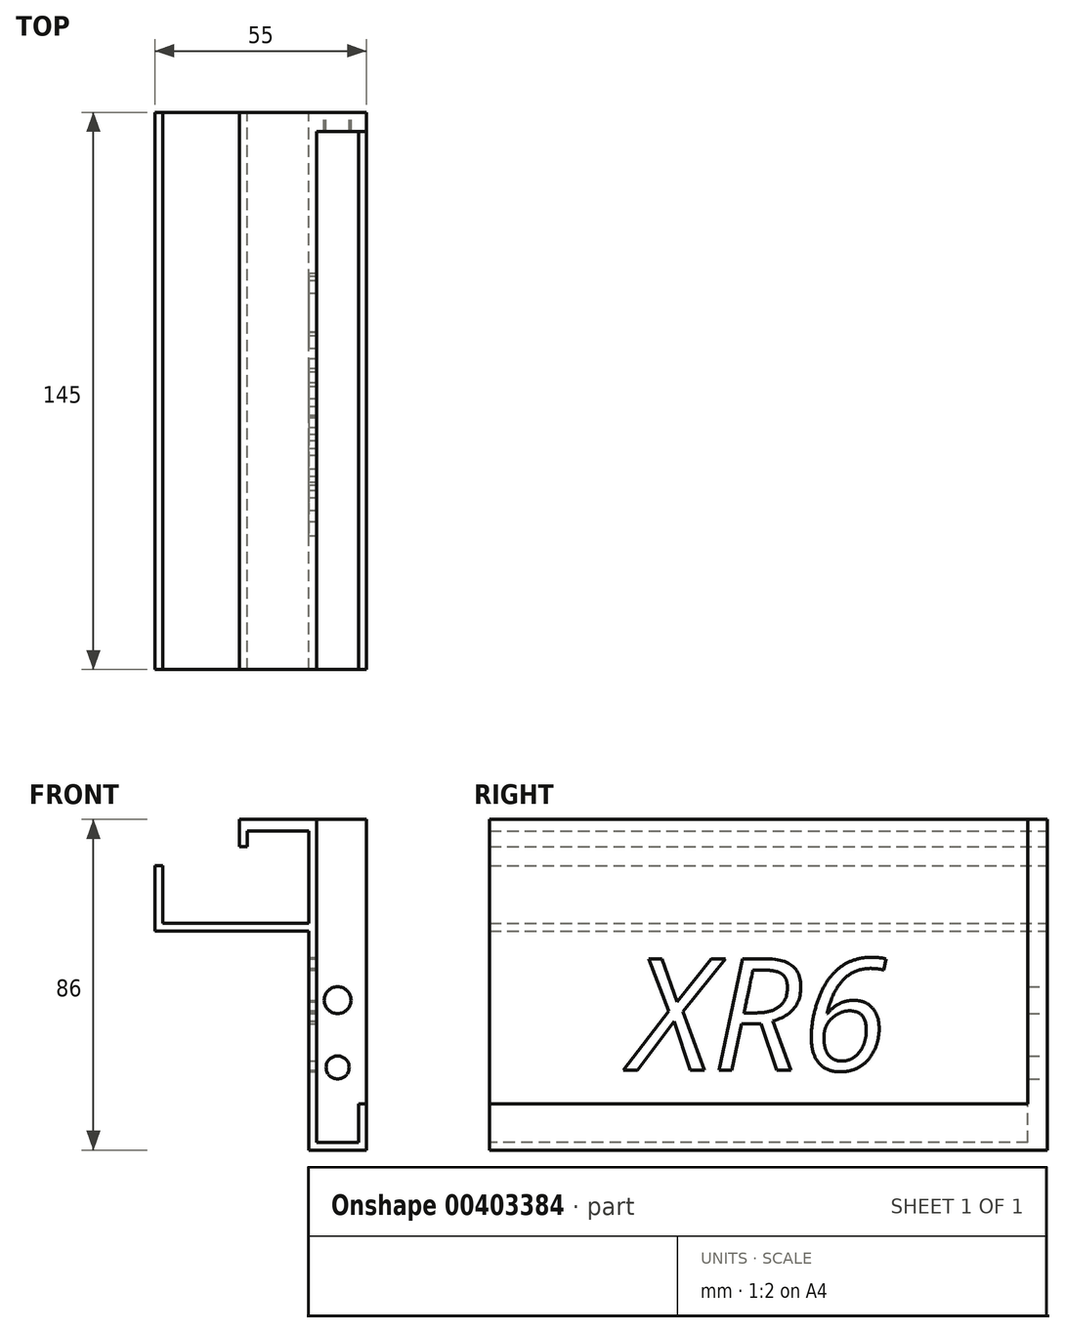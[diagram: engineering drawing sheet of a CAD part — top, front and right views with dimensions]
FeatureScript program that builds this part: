
annotation { "Feature Type Name" : "Feature", "Feature Type Description" : "" }
export const myFeature = defineFeature(function(context is Context, id is Id, definition is map)
    precondition{}
    {
        {
            var Q0;
            Q0=qCreatedBy(makeId("Front.planeOp"),FACE);
            var sketch = newSketch(context, id + "F0", { "sketchPlane" : qUnion([Q0])});
            skLineSegment(sketch, "E0", {"start": v(0, -43) * mm, "end": v(15, -43) * mm});
            skLineSegment(sketch, "E1", {"start": v(15, -43) * mm, "end": v(15, -31) * mm});
            skLineSegment(sketch, "E2", {"start": v(2, 43) * mm, "end": v(-18, 43) * mm});
            skLineSegment(sketch, "E3", {"start": v(-18, 43) * mm, "end": v(-18, 36) * mm});
            skLineSegment(sketch, "E4", {"start": v(-18, 36) * mm, "end": v(-16, 36) * mm});
            skLineSegment(sketch, "E5", {"start": v(-16, 36) * mm, "end": v(-16, 40) * mm});
            skLineSegment(sketch, "E6", {"start": v(-16, 40) * mm, "end": v(0, 40) * mm});
            skLineSegment(sketch, "E7", {"start": v(0, 40) * mm, "end": v(0, 16) * mm});
            skLineSegment(sketch, "E8", {"start": v(0, 16) * mm, "end": v(-38, 16) * mm});
            skLineSegment(sketch, "E9", {"start": v(-38, 16) * mm, "end": v(-38, 31) * mm});
            skLineSegment(sketch, "E10", {"start": v(-38, 31) * mm, "end": v(-40, 31) * mm});
            skLineSegment(sketch, "E11", {"start": v(-40, 31) * mm, "end": v(-40, 14) * mm});
            skLineSegment(sketch, "E12", {"start": v(-40, 14) * mm, "end": v(0, 14) * mm});
            skLineSegment(sketch, "E13", {"start": v(0, 14) * mm, "end": v(0, -43) * mm});
            skLineSegment(sketch, "E14", {"start": v(15, -31) * mm, "end": v(2, -31) * mm});
            skLineSegment(sketch, "E15", {"start": v(2, -31) * mm, "end": v(2, 43) * mm});
            skSolve(sketch);
        }
        {
            var Q0;
            Q0=makeQuery(id+"F0.imprint","IMPRINT",FACE,{"disambiguationData":[TD([[makeQuery(id+"F0.imprint","IMPRINT",EDGE,{"derivedFrom":sQuery(id+"F0.wireOp",EDGE,"E0")}),1.0]])]});
            extrude(context, id + "F1", {"entities" : qUnion([Q0]), "depth" : 145 * mm});
        }
        {
            var Q0;
            Q0=makeQuery(id+"F1.opExtrude","CAP_FACE",FACE,{"disambiguationData":[OSD([sQuery(id+"F0.wireOp",EDGE,"E0"),sQuery(id+"F0.wireOp",EDGE,"E1"),sQuery(id+"F0.wireOp",EDGE,"E2"),sQuery(id+"F0.wireOp",EDGE,"E3"),sQuery(id+"F0.wireOp",EDGE,"E4"),sQuery(id+"F0.wireOp",EDGE,"E5"),sQuery(id+"F0.wireOp",EDGE,"E6"),sQuery(id+"F0.wireOp",EDGE,"E7"),sQuery(id+"F0.wireOp",EDGE,"E8"),sQuery(id+"F0.wireOp",EDGE,"E9"),sQuery(id+"F0.wireOp",EDGE,"E10"),sQuery(id+"F0.wireOp",EDGE,"E11"),sQuery(id+"F0.wireOp",EDGE,"E12"),sQuery(id+"F0.wireOp",EDGE,"E13"),sQuery(id+"F0.wireOp",EDGE,"E14"),sQuery(id+"F0.wireOp",EDGE,"E15")])],"isStart":false});
            var sketch = newSketch(context, id + "F2", { "sketchPlane" : qUnion([Q0])});
            skLineSegment(sketch, "E16", {"start": v(13, -31) * mm, "end": v(13, -41) * mm});
            skLineSegment(sketch, "E17", {"start": v(13, -41) * mm, "end": v(2, -41) * mm});
            skLineSegment(sketch, "E18", {"start": v(2, -41) * mm, "end": v(2, -31) * mm});
            skLineSegment(sketch, "E19", {"start": v(2, -31) * mm, "end": v(13, -31) * mm});
            skSolve(sketch);
        }
        {
            var Q0;
            Q0=makeQuery(id+"F2.imprint","IMPRINT",FACE,{"disambiguationData":[TD([[makeQuery(id+"F2.imprint","IMPRINT",EDGE,{"derivedFrom":sQuery(id+"F2.wireOp",EDGE,"E16")}),-1.0]])]});
            extrude(context, id + "F3", {"entities" : qUnion([Q0]), "operationType" : NewBodyOperationType.REMOVE, "oppositeDirection" : true, "depth" : 140 * mm});
        }
        {
            var Q0;
            Q0=makeQuery(id+"F3.boolean.opBoolean","MERGE",FACE,{"derivedFrom":[makeQuery(id+"F1.opExtrude","SWEPT_FACE",FACE,{"disambiguationData":[OSD([sQuery(id+"F0.wireOp",EDGE,"E15")])]}),makeQuery(id+"F3.opExtrude","SWEPT_FACE",FACE,{"disambiguationData":[OSD([sQuery(id+"F2.wireOp",EDGE,"E18")])]})]});
            var sketch = newSketch(context, id + "F4", { "sketchPlane" : qUnion([Q0])});
            skLineSegment(sketch, "E20", {"start": v(0, 43) * mm, "end": v(-5, 43) * mm});
            skSolve(sketch);
        }
        {
            var Q0;
            {var subQ4=sQuery(id+"F4.wireOp",EDGE,"E20");Q0=makeQuery(id+"F4.imprint","IMPRINT",FACE,{"disambiguationData":[TD([[makeQuery(id+"F4.imprint","IMPRINT",EDGE,{"derivedFrom":subQ4}),-1.0]])]});}
            var sketch = newSketch(context, id + "F5", { "sketchPlane" : qUnion([Q0])});
            skLineSegment(sketch, "E21", {"start": v(0, 43.34) * mm, "end": v(-5, 43.34) * mm});
            skLineSegment(sketch, "E22", {"start": v(-5, 43.34) * mm, "end": v(-5, -26.66) * mm});
            skLineSegment(sketch, "E23", {"start": v(-5, -26.66) * mm, "end": v(0, -26.66) * mm});
            skSolve(sketch);
        }
        {
            var Q0;
            {var subQ5=sQuery(id+"F5.wireOp",EDGE,"E23");Q0=makeQuery(id+"F5.imprint","IMPRINT",FACE,{"disambiguationData":[TD([[makeQuery(id+"F5.imprint","IMPRINT",EDGE,{"derivedFrom":subQ5}),1.0]])]});}
            extrude(context, id + "F6", {"entities" : qUnion([Q0]), "operationType" : NewBodyOperationType.ADD, "depth" : 13 * mm});
        }
        {
            var Q0;
            {var subQ0=sQuery(id+"F0.wireOp",EDGE,"E15");Q0=makeQuery(id+"F6.boolean.opBoolean","MERGE",FACE,{"derivedFrom":[makeQuery(id+"F1.opExtrude","CAP_FACE",FACE,{"disambiguationData":[OSD([sQuery(id+"F0.wireOp",EDGE,"E0"),sQuery(id+"F0.wireOp",EDGE,"E1"),sQuery(id+"F0.wireOp",EDGE,"E2"),sQuery(id+"F0.wireOp",EDGE,"E3"),sQuery(id+"F0.wireOp",EDGE,"E4"),sQuery(id+"F0.wireOp",EDGE,"E5"),sQuery(id+"F0.wireOp",EDGE,"E6"),sQuery(id+"F0.wireOp",EDGE,"E7"),sQuery(id+"F0.wireOp",EDGE,"E8"),sQuery(id+"F0.wireOp",EDGE,"E9"),sQuery(id+"F0.wireOp",EDGE,"E10"),sQuery(id+"F0.wireOp",EDGE,"E11"),sQuery(id+"F0.wireOp",EDGE,"E12"),sQuery(id+"F0.wireOp",EDGE,"E13"),sQuery(id+"F0.wireOp",EDGE,"E14"),subQ0])],"isStart":true}),makeQuery(id+"F6.opExtrude","SWEPT_FACE",FACE,{"disambiguationData":[OSD([subQ0])]})]});}
            var sketch = newSketch(context, id + "F7", { "sketchPlane" : qUnion([Q0])});
            skCircle(sketch, "E24", {"center": v(-7.5, -21.5) * mm, "radius": 3 * mm});
            skCircle(sketch, "E25", {"center": v(-7.5, -4) * mm, "radius": 3.5 * mm});
            skSolve(sketch);
        }
        {
            var Q0;
            Q0=makeQuery(id+"F7.imprint","IMPRINT",FACE,{"disambiguationData":[TD([[makeQuery(id+"F7.imprint","IMPRINT",EDGE,{"derivedFrom":sQuery(id+"F7.wireOp",EDGE,"E25")}),1.0]])]});
            var Q1;
            Q1=makeQuery(id+"F7.imprint","IMPRINT",FACE,{"disambiguationData":[TD([[makeQuery(id+"F7.imprint","IMPRINT",EDGE,{"derivedFrom":sQuery(id+"F7.wireOp",EDGE,"E24")}),1.0]])]});
            extrude(context, id + "F8", {"entities" : qUnion([Q0, Q1]), "operationType" : NewBodyOperationType.REMOVE, "oppositeDirection" : true, "depth" : 6 * mm});
        }
        {
            var Q0;
            {var subQ0=sQuery(id+"F0.wireOp",EDGE,"E15");Q0=makeQuery(id+"F6.boolean.opBoolean","MERGE",FACE,{"derivedFrom":[makeQuery(id+"F1.opExtrude","CAP_FACE",FACE,{"disambiguationData":[OSD([sQuery(id+"F0.wireOp",EDGE,"E0"),sQuery(id+"F0.wireOp",EDGE,"E1"),sQuery(id+"F0.wireOp",EDGE,"E2"),sQuery(id+"F0.wireOp",EDGE,"E3"),sQuery(id+"F0.wireOp",EDGE,"E4"),sQuery(id+"F0.wireOp",EDGE,"E5"),sQuery(id+"F0.wireOp",EDGE,"E6"),sQuery(id+"F0.wireOp",EDGE,"E7"),sQuery(id+"F0.wireOp",EDGE,"E8"),sQuery(id+"F0.wireOp",EDGE,"E9"),sQuery(id+"F0.wireOp",EDGE,"E10"),sQuery(id+"F0.wireOp",EDGE,"E11"),sQuery(id+"F0.wireOp",EDGE,"E12"),sQuery(id+"F0.wireOp",EDGE,"E13"),sQuery(id+"F0.wireOp",EDGE,"E14"),subQ0])],"isStart":true}),makeQuery(id+"F6.opExtrude","SWEPT_FACE",FACE,{"disambiguationData":[OSD([subQ0])]})]});}
            var sketch = newSketch(context, id + "F9", { "sketchPlane" : qUnion([Q0])});
            skLineSegment(sketch, "E26", {"start": v(-15, -26.66) * mm, "end": v(-15, -31) * mm});
            skLineSegment(sketch, "E27", {"start": v(-15, -31) * mm, "end": v(-2, -31) * mm});
            skLineSegment(sketch, "E28", {"start": v(-2, -31) * mm, "end": v(-2, -26.66) * mm});
            skLineSegment(sketch, "E29", {"start": v(-2, -26.66) * mm, "end": v(-15, -26.66) * mm});
            skSolve(sketch);
        }
        {
            var Q0;
            Q0=makeQuery(id+"F9.imprint","IMPRINT",FACE,{"disambiguationData":[TD([[makeQuery(id+"F9.imprint","IMPRINT",EDGE,{"derivedFrom":sQuery(id+"F9.wireOp",EDGE,"E26")}),1.0]])]});
            extrude(context, id + "F10", {"entities" : qUnion([Q0]), "operationType" : NewBodyOperationType.ADD, "oppositeDirection" : true, "depth" : 5 * mm});
        }
        {
            var Q0;
            {var subQ4=sQuery(id+"F4.wireOp",EDGE,"E20");Q0=makeQuery(id+"F4.imprint","IMPRINT",FACE,{"disambiguationData":[TD([[makeQuery(id+"F4.imprint","IMPRINT",EDGE,{"derivedFrom":subQ4}),-1.0]])]});}
            var sketch = newSketch(context, id + "F11", { "sketchPlane" : qUnion([Q0])});
            skText(sketch, "E30", { "text": "XR6", "fontName": "OpenSans-Italic.ttf"});
            const initialGuessF11  = {"E30": [-0.10815, -0.02225, 1, 0, 0.02924]};
            skSetInitialGuess(sketch, initialGuessF11);
            skSolve(sketch);
        }
        {
            var Q0;
            Q0 = qSketchRegion(id + "F11", true);
            var Q1;
            Q1 = qConstructionFilter(qBodyType(qCreatedBy(id + "F11" ,EDGE), BodyType.WIRE), ConstructionObject.NO);
            extrude(context, id + "F12", {"entities" : qUnion([Q0]), "operationType" : NewBodyOperationType.REMOVE, "surfaceEntities" : qUnion([Q1]), "oppositeDirection" : true, "depth" : 5 * mm});
        }
    });
